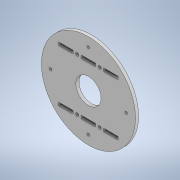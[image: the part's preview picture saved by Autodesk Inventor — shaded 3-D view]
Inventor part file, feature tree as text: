
AUTODESK INVENTOR PART (.ipt)
format: ipt  version: 2022 (Build 260153000, 153)  size: 178,176 bytes
history: native  units: mm
features: extrude x1, sketch x1
ambient origin geometry x8: Origin, YZ Plane, XZ Plane, XY Plane, X Axis, Y Axis, Z Axis, Center Point
bodies: Body1 (feature_tree)
feature tree (2):
  extrude  "Extrusion2"  Depth=22.0mm
  sketch  "Sketch3"  dims[d32=2.5mm d33=2.5mm d34=2.5mm d35=2.5mm d45=3.1mm d46=3.1mm d47=3.1mm d50=14.0mm d51=4.0mm d53=14.0mm d54=4.0mm d57=14.0mm d58=14.0mm d59=14.0mm d60=3.0mm d61=14.0mm d62=3.0mm d63=0.0mm d64=3.0mm d65=3.0mm d71=1.5mm d72=1.5mm d74=92.0mm d75=74.0mm d78=24.6mm d80=3.1mm d81=25.5mm d82=25.5mm d83=22.0mm d84=11.0mm d87=4.0mm d91=22.0mm d92=1.5mm d93=1.5mm d94=1.5mm d95=1.5mm d96=1.5mm d97=1.5mm d98=4.0mm]
